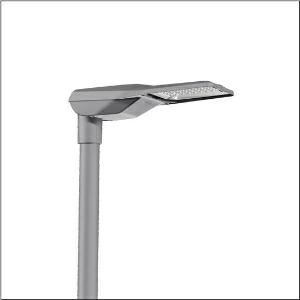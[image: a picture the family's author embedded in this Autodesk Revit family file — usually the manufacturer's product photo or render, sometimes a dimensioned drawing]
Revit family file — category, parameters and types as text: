
# Revit family: streetlight_sl_21_iq_mini___st1_0a_5xe2d61g08hb_24ab
name_source: partatom
category: Lighting Fixtures
units: mm (PartAtom-declared; Revit-internal decimal feet)

## family parameters
Cut with Voids When Loaded = No
Host = Face
Light Source = No
Part Type = Normal
Room Calculation Point = No
Round Connector Dimension = Use Diameter
Shared = No

## types (1)
- --- (1 x LED, 8480 lm, 70.9 W, 2700K)
    Apparent Load = 71 VA
    CIE Flux Codes = 37 72 97 100 100
    Color Rendering = 70
    Color Temperature = 2700K
    Default Elevation = 1800 mm
    Description = Streetlight SL 21 iQ mini, mast luminaire, primary light control with lens, of PMMA, primary optical cover: cover, of toughened safety glass, transparent, light distribution: ST1.0a, light emission: direct distribution, primary light characteristic: asymmetric, installation type: post-top, side-entry, LED, High Power LED, rated luminous flux: 8.480lm, luminous efficacy: 120lm/W, light colour: 727, colour temperature: 2700K, control: Street-Remote, Auto-Match, Temp-Guard, Lumen-Switch, Night-Set, Smart-Wire, Light-Fading, Desk-Remote (wireless, voltage-free reading and setting of iQ features in the workshop via application-optimized NFC function/RFID function), optimised constant luminous flux control (CLO 2.0), presetting dimming linear, mains connection: 220..240V, AC, 50/60Hz, start of lifetime: 71W, end of service life: 75W, reduction: 31W, luminaire housing, of diecast aluminium, powder-coated, Siteco® metallic grey (DB 702S), corrosivity category C5 mid according to DIN EN ISO 12944, please order mast flange separately, inclination adjustable: 0°, 5°, 10°, 15°, sealing non-destructively replaceable, multi-level sealing system, length: 628mm, width: 235mm, height: 110mm, mast flange for spigot size: 42mm (side-entry): 5XC10008XM4, 60/48mm (side-entry/post-top): 5XC10108XM2, 76/60mm (side-entry/post-top): 5XC10108XM1, protection rating (complete): IP66, insulation class (complete): insulation class II (safety insulation), certification: CE, ENEC, ENEC+, VDE, impact resistance: IK09, permissible operating ambient temperature for outdoor applications: -40..+50°C, standard-compliant lighting for roads and squares, packaging unit: 1 piece

Light Distribution: ST1.0a
    Height = 110 mm
    Lamp = 1 x LED
    Lamp Light Flux = 8480 lm
    Lamp Power = 70.9 W
    Lamp count = 1
    Length = 625 mm
    Luminous efficacy = 120 lm/W
    Manufacturer = Siteco
    ModVariant = No
    Model = 5XE2D61G08HB
    Number of Poles = 1
    OnlyDefault = Yes
    Power Factor = 1
    Product Name = Streetlight SL 21 iQ mini | ST1.0a
    Product group = mast luminaire | pylon top
    ProductGroupID = 6100
    Protection Class = Protection class II
    Protection Degree = IP 66
    RLX_Detail_Level = 1
    RLX_Emergency_Light_Flux = 0 lm
    RLX_Emergency_Type = 0
    RLX_Emergency_Type_DB = No
    RlxData = <blob elided: 92449 chars, md5=3ad4861a>
    Socket = socket
    Standby Power = 0 W
    System Light Flux = 8480 lm
    System Power = 71 W
    Type Comments = factory setting: luminous flux: 100 % | dim-lin: 254 | 711 mA
    Type Image = l_1003519.jpg
    URL = http://relux.com
    VarID = @adj_090533
    Voltage = 0 V
    Weight = 0.00 kg
    Width = 234 mm

## geometry (parser evidence)
native form markers: Blend x4, Sweep x13
no freeform markers — native parametric forms only
